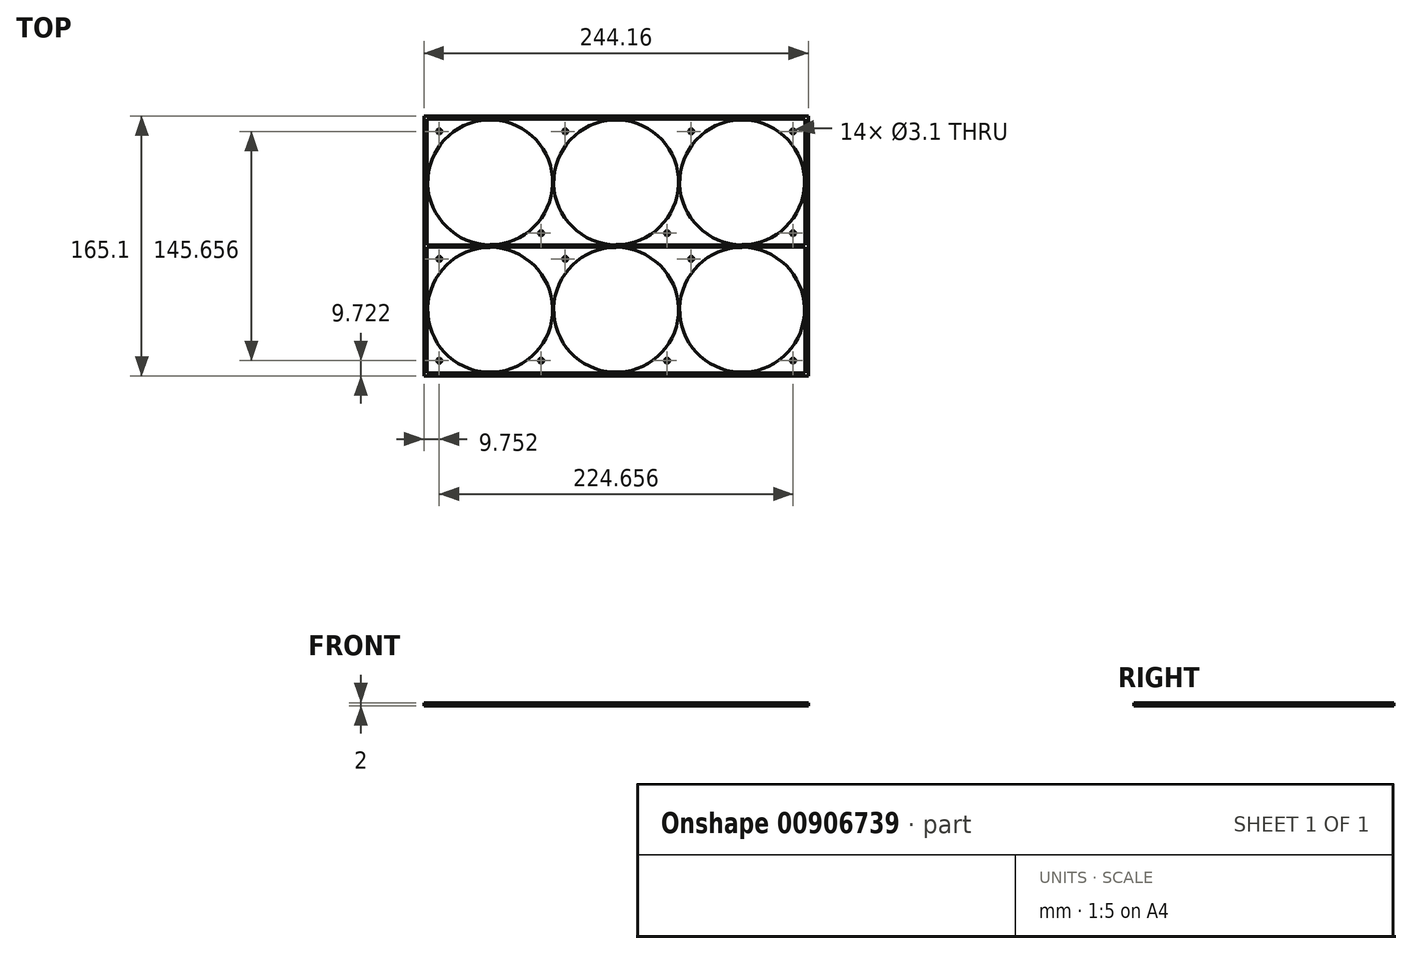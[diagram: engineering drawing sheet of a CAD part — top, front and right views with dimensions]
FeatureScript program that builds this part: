
annotation { "Feature Type Name" : "Feature", "Feature Type Description" : "" }
export const myFeature = defineFeature(function(context is Context, id is Id, definition is map)
    precondition{}
    {
        {
            assignVariable(context, id + "F0", {"name" : "wirethickness", "anyValue" : 1.3 * mm});
        }
        {
            var Q0;
            Q0=qCreatedBy(makeId("Top.planeOp"),FACE);
            var sketch = newSketch(context, id + "F1", { "sketchPlane" : qUnion([Q0])});
            skLineSegment(sketch, "E0.bottom", {"start": v(-122.07, 82.55) * mm, "end": v(122.08, 82.55) * mm});
            skLineSegment(sketch, "E0.top", {"start": v(-122.08, -82.55) * mm, "end": v(122.07, -82.55) * mm});
            skLineSegment(sketch, "E0.left", {"start": v(-122.07, 82.55) * mm, "end": v(-122.08, -82.55) * mm});
            skLineSegment(sketch, "E0.right", {"start": v(122.08, 82.55) * mm, "end": v(122.07, -82.55) * mm});
            skPoint(sketch, "E0.middle", {"position": v(0, 0) * mm});
            skSolve(sketch);
        }
        {
            var Q0;
            Q0=qSketchRegion(id+"F1",true);
            extrude(context, id + "F2", {"entities" : qUnion([Q0]), "depth" : 2 * mm, "offsetDistance" : 25 * mm});
        }
        {
            var Q0;
            Q0=makeQuery(id+"F2.opExtrude","CAP_FACE",FACE,{"disambiguationData":[OSD([sQuery(id+"F1.wireOp",EDGE,"E0.bottom"),sQuery(id+"F1.wireOp",EDGE,"E0.top"),sQuery(id+"F1.wireOp",EDGE,"E0.left"),sQuery(id+"F1.wireOp",EDGE,"E0.right")])],"isStart":false});
            var sketch = newSketch(context, id + "F3", { "sketchPlane" : qUnion([Q0])});
            skLineSegment(sketch, "E1", {"start": v(-120.07, 80.55) * mm, "end": v(-120.08, 1) * mm});
            skLineSegment(sketch, "E2", {"start": v(120.07, -80.55) * mm, "end": v(120.08, -1) * mm});
            skLineSegment(sketch, "E3", {"start": v(-120.07, 80.55) * mm, "end": v(120.08, 80.55) * mm});
            skLineSegment(sketch, "E4", {"start": v(-120.08, -80.55) * mm, "end": v(120.07, -80.55) * mm});
            skLineSegment(sketch, "E5", {"start": v(-120.08, 0.5) * mm, "end": v(120.08, 0.5) * mm});
            skLineSegment(sketch, "E6", {"start": v(-120.08, -0.5) * mm, "end": v(120.08, -0.5) * mm});
            skLineSegment(sketch, "E7.trimOffspring", {"start": v(120.08, 1) * mm, "end": v(120.08, 80.55) * mm});
            skLineSegment(sketch, "E8.trimOffspring", {"start": v(-120.08, -1) * mm, "end": v(-120.08, -80.55) * mm});
            skLineSegment(sketch, "E9", {"start": v(120.08, 1) * mm, "end": v(120.08, 0.5) * mm});
            skLineSegment(sketch, "E10", {"start": v(-120.08, 1) * mm, "end": v(-120.08, 0.5) * mm});
            skLineSegment(sketch, "E11", {"start": v(-120.08, -0.5) * mm, "end": v(-120.08, -1) * mm});
            skLineSegment(sketch, "E12", {"start": v(120.08, -1) * mm, "end": v(120.08, -0.5) * mm});
            skSolve(sketch);
        }
        {
            var Q0;
            Q0=qSketchRegion(id+"F3",true);
            extrude(context, id + "F4", {"entities" : qUnion([Q0]), "operationType" : NewBodyOperationType.REMOVE, "oppositeDirection" : true, "depth" : 0.26 * mm, "offsetDistance" : 25 * mm});
        }
        {
            var Q0;
            Q0=makeQuery(id+"F2.opExtrude","CAP_FACE",FACE,{"disambiguationData":[OSD([sQuery(id+"F1.wireOp",EDGE,"E0.bottom"),sQuery(id+"F1.wireOp",EDGE,"E0.top"),sQuery(id+"F1.wireOp",EDGE,"E0.left"),sQuery(id+"F1.wireOp",EDGE,"E0.right")])],"isStart":true});
            var sketch = newSketch(context, id + "F5", { "sketchPlane" : qUnion([Q0])});
            skLineSegment(sketch, "E13", {"start": v(-40, 0.5) * mm, "end": v(-40, 80.55) * mm});
            skLineSegment(sketch, "E14", {"start": v(40, 0.5) * mm, "end": v(40, 80.55) * mm});
            skCircle(sketch, "E15", {"center": v(-47.67, 72.83) * mm, "radius": 1.55 * mm});
            skCircle(sketch, "E16", {"center": v(32.33, 72.83) * mm, "radius": 1.55 * mm});
            skCircle(sketch, "E17", {"center": v(112.33, 72.83) * mm, "radius": 1.55 * mm});
            skCircle(sketch, "E18", {"center": v(-112.33, 8.17) * mm, "radius": 1.55 * mm});
            skCircle(sketch, "E19", {"center": v(-32.33, 8.17) * mm, "radius": 1.55 * mm});
            skCircle(sketch, "E20", {"center": v(47.67, 8.17) * mm, "radius": 1.55 * mm});
            skCircle(sketch, "E21", {"center": v(-112.33, -72.83) * mm, "radius": 1.55 * mm});
            skCircle(sketch, "E22", {"center": v(-32.33, -72.83) * mm, "radius": 1.55 * mm});
            skCircle(sketch, "E23", {"center": v(47.67, -72.83) * mm, "radius": 1.55 * mm});
            skCircle(sketch, "E24", {"center": v(112.33, -8.17) * mm, "radius": 1.55 * mm});
            skCircle(sketch, "E25", {"center": v(32.33, -8.17) * mm, "radius": 1.55 * mm});
            skCircle(sketch, "E26", {"center": v(-47.67, -8.17) * mm, "radius": 1.55 * mm});
            skCircle(sketch, "E27", {"center": v(112.33, -72.83) * mm, "radius": 1.55 * mm});
            skCircle(sketch, "E28", {"center": v(-112.33, 72.83) * mm, "radius": 1.55 * mm});
            skSolve(sketch);
        }
        {
            var Q0;
            Q0=qSketchRegion(id+"F5",true);
            extrude(context, id + "F6", {"entities" : qUnion([Q0]), "operationType" : NewBodyOperationType.REMOVE, "endBound" : BoundingType.THROUGH_ALL, "oppositeDirection" : true, "depth" : 25 * mm, "offsetDistance" : 25 * mm});
        }
        {
            var Q0;
            Q0=makeQuery(id+"F2.opExtrude","CAP_FACE",FACE,{"disambiguationData":[OSD([sQuery(id+"F1.wireOp",EDGE,"E0.bottom"),sQuery(id+"F1.wireOp",EDGE,"E0.top"),sQuery(id+"F1.wireOp",EDGE,"E0.left"),sQuery(id+"F1.wireOp",EDGE,"E0.right")])],"isStart":false});
            var sketch = newSketch(context, id + "F7", { "sketchPlane" : qUnion([Q0])});
            skCircle(sketch, "E29", {"center": v(-80, -40.5) * mm, "radius": 39.65 * mm});
            skCircle(sketch, "E30", {"center": v(0, -40.5) * mm, "radius": 39.65 * mm});
            skCircle(sketch, "E31", {"center": v(80, -40.5) * mm, "radius": 39.65 * mm});
            skCircle(sketch, "E32", {"center": v(-80, 40.5) * mm, "radius": 39.65 * mm});
            skCircle(sketch, "E33", {"center": v(0, 40.5) * mm, "radius": 39.65 * mm});
            skCircle(sketch, "E34", {"center": v(80, 40.5) * mm, "radius": 39.65 * mm});
            skLineSegment(sketch, "E35.bottom", {"start": v(83.9, -0.5) * mm, "end": v(80, -0.5) * mm});
            skLineSegment(sketch, "E35.top", {"start": v(83.9, -1.06) * mm, "end": v(80, -1.06) * mm});
            skLineSegment(sketch, "E35.left", {"start": v(83.9, -0.5) * mm, "end": v(83.9, -1.06) * mm});
            skLineSegment(sketch, "E35.right", {"start": v(80, -0.5) * mm, "end": v(80, -1.06) * mm});
            skLineSegment(sketch, "E36.bottom", {"start": v(76.1, 0.5) * mm, "end": v(80, 0.5) * mm});
            skLineSegment(sketch, "E36.top", {"start": v(76.1, 1.07) * mm, "end": v(80, 1.07) * mm});
            skLineSegment(sketch, "E36.left", {"start": v(76.1, 0.5) * mm, "end": v(76.1, 1.07) * mm});
            skLineSegment(sketch, "E36.right", {"start": v(80, 0.5) * mm, "end": v(80, 1.07) * mm});
            skLineSegment(sketch, "E37.bottom", {"start": v(3.9, -0.5) * mm, "end": v(0, -0.5) * mm});
            skLineSegment(sketch, "E37.top", {"start": v(3.9, -1.07) * mm, "end": v(0, -1.07) * mm});
            skLineSegment(sketch, "E37.left", {"start": v(3.9, -0.5) * mm, "end": v(3.9, -1.07) * mm});
            skLineSegment(sketch, "E37.right", {"start": v(0, -0.5) * mm, "end": v(0, -1.07) * mm});
            skLineSegment(sketch, "E38.bottom", {"start": v(-3.9, 0.5) * mm, "end": v(0, 0.5) * mm});
            skLineSegment(sketch, "E38.top", {"start": v(-3.9, 1.06) * mm, "end": v(0, 1.06) * mm});
            skLineSegment(sketch, "E38.left", {"start": v(-3.9, 0.5) * mm, "end": v(-3.9, 1.06) * mm});
            skLineSegment(sketch, "E38.right", {"start": v(0, 0.5) * mm, "end": v(0, 1.06) * mm});
            skLineSegment(sketch, "E39.bottom", {"start": v(-76.1, -0.5) * mm, "end": v(-80, -0.5) * mm});
            skLineSegment(sketch, "E39.top", {"start": v(-76.1, -1.07) * mm, "end": v(-80, -1.07) * mm});
            skLineSegment(sketch, "E39.left", {"start": v(-76.1, -0.5) * mm, "end": v(-76.1, -1.07) * mm});
            skLineSegment(sketch, "E39.right", {"start": v(-80, -0.5) * mm, "end": v(-80, -1.07) * mm});
            skLineSegment(sketch, "E40.bottom", {"start": v(-83.9, 0.5) * mm, "end": v(-80, 0.5) * mm});
            skLineSegment(sketch, "E40.top", {"start": v(-83.9, 1.06) * mm, "end": v(-80, 1.06) * mm});
            skLineSegment(sketch, "E40.left", {"start": v(-83.9, 0.5) * mm, "end": v(-83.9, 1.06) * mm});
            skLineSegment(sketch, "E40.right", {"start": v(-80, 0.5) * mm, "end": v(-80, 1.06) * mm});
            skSolve(sketch);
        }
        {
            var Q0;
            Q0 = qSketchRegion(id + "F7", true);
            extrude(context, id + "F8", {"entities" : qUnion([Q0]), "operationType" : NewBodyOperationType.REMOVE, "oppositeDirection" : true, "depth" : 0.66 * mm, "offsetDistance" : 25 * mm});
        }
        {
            var Q0;
            Q0=makeQuery(id+"F8.boolean.opBoolean","COPY",EDGE,{"derivedFrom":makeQuery(id+"F8.opExtrude","CAP_EDGE",EDGE,{"disambiguationData":[OSD([sQuery(id+"F7.wireOp",EDGE,"E33")])],"isStart":false})});
            var Q1;
            Q1=makeQuery(id+"F8.boolean.opBoolean","COPY",EDGE,{"derivedFrom":makeQuery(id+"F8.opExtrude","CAP_EDGE",EDGE,{"disambiguationData":[OSD([sQuery(id+"F7.wireOp",EDGE,"E32")])],"isStart":false})});
            var Q2;
            Q2=makeQuery(id+"F8.boolean.opBoolean","COPY",EDGE,{"derivedFrom":makeQuery(id+"F8.opExtrude","CAP_EDGE",EDGE,{"disambiguationData":[OSD([sQuery(id+"F7.wireOp",EDGE,"E34")])],"isStart":false})});
            var Q3;
            Q3=makeQuery(id+"F8.boolean.opBoolean","COPY",EDGE,{"derivedFrom":makeQuery(id+"F8.opExtrude","CAP_EDGE",EDGE,{"disambiguationData":[OSD([sQuery(id+"F7.wireOp",EDGE,"E30")])],"isStart":false})});
            var Q4;
            Q4=makeQuery(id+"F8.boolean.opBoolean","COPY",EDGE,{"derivedFrom":makeQuery(id+"F8.opExtrude","CAP_EDGE",EDGE,{"disambiguationData":[OSD([sQuery(id+"F7.wireOp",EDGE,"E31")])],"isStart":false})});
            var Q5;
            Q5=makeQuery(id+"F8.boolean.opBoolean","COPY",EDGE,{"derivedFrom":makeQuery(id+"F8.opExtrude","CAP_EDGE",EDGE,{"disambiguationData":[OSD([sQuery(id+"F7.wireOp",EDGE,"E29")])],"isStart":false})});
            fillet(context, id + "F9", {"entities" : qUnion([Q0, Q1, Q2, Q3, Q4, Q5]), "radius" : getVariable(context, 'wirethickness') / 2, "tangentPropagation" : true, "allowEdgeOverflow" : false});
        }
    });
